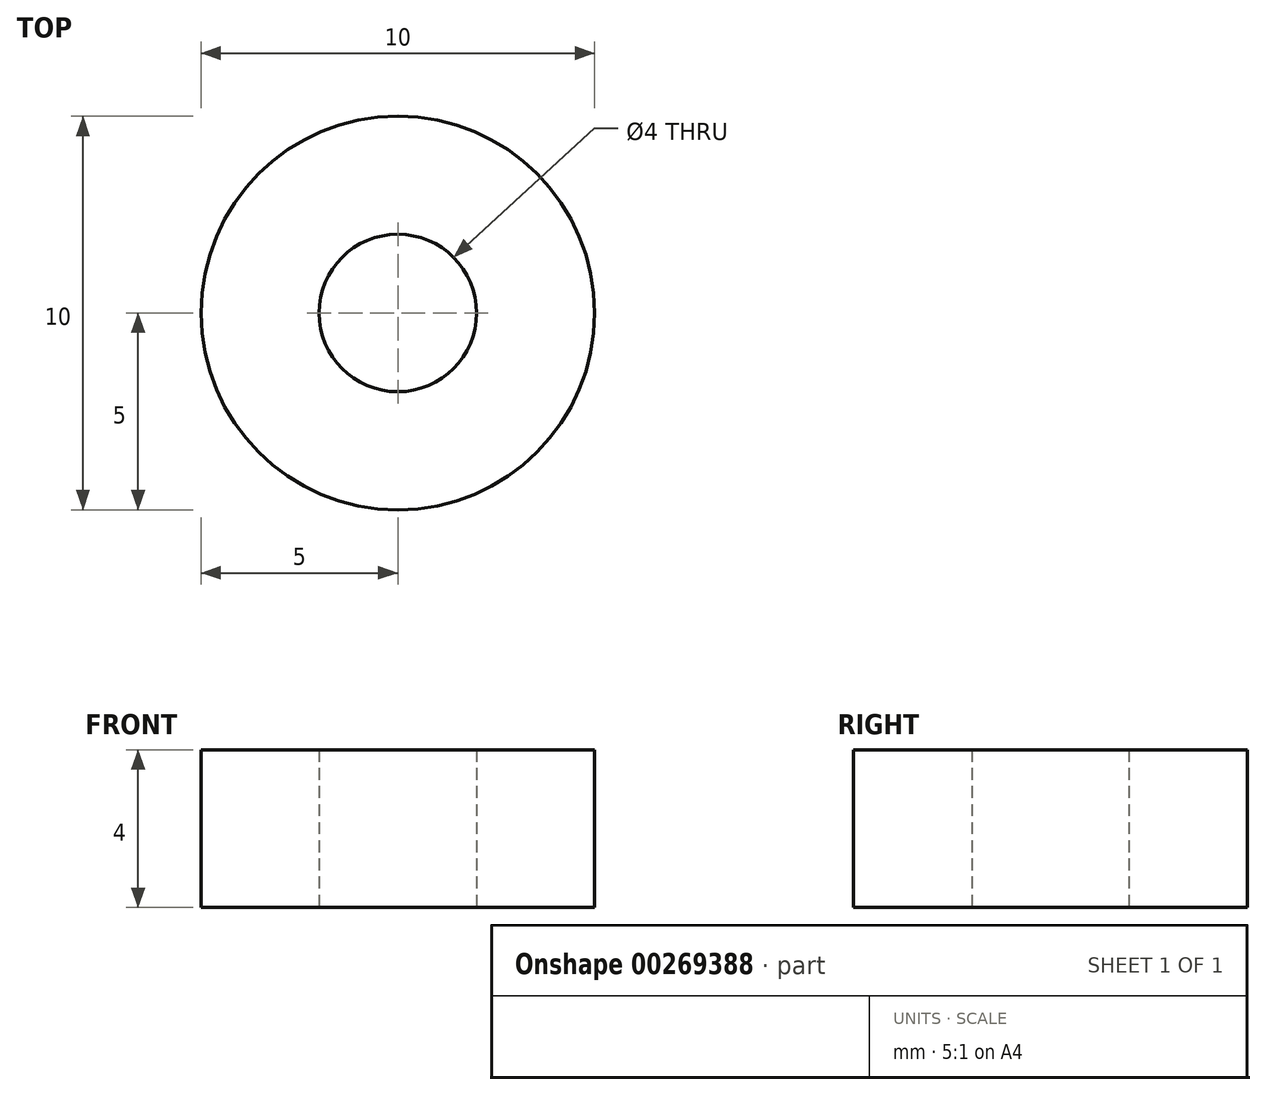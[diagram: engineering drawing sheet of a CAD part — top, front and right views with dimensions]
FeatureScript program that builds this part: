
annotation { "Feature Type Name" : "Feature", "Feature Type Description" : "" }
export const myFeature = defineFeature(function(context is Context, id is Id, definition is map)
    precondition{}
    {
        {
            var Q0;
            Q0=qCreatedBy(makeId("Top.planeOp"),FACE);
            var sketch = newSketch(context, id + "F0", { "sketchPlane" : qUnion([Q0])});
            skCircle(sketch, "E0", {"center": v(0, 0) * mm, "radius": 5 * mm});
            skCircle(sketch, "E1", {"center": v(0, 0) * mm, "radius": 2 * mm});
            skSolve(sketch);
        }
        {
            var Q0;
            Q0=makeQuery(id+"F0.imprint","IMPRINT",FACE,{"disambiguationData":[TD([[makeQuery(id+"F0.imprint","IMPRINT",EDGE,{"derivedFrom":sQuery(id+"F0.wireOp",EDGE,"E0")}),1.0]])]});
            extrude(context, id + "F1", {"entities" : qUnion([Q0]), "endBound" : BoundingType.SYMMETRIC, "depth" : 4 * mm});
        }
    });
